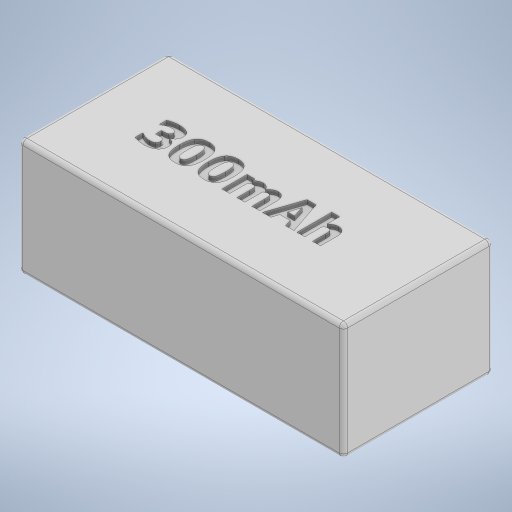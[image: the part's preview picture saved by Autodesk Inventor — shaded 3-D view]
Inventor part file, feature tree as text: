
AUTODESK INVENTOR PART (.ipt)
format: ipt  version: 2023.5 (Build 275446000, 446)  size: 368,640 bytes
history: native  units: mm
features: extrude x2, sketch x2, other x1, fillet x1
ambient origin geometry x8: Origin, YZ Plane, XZ Plane, XY Plane, X Axis, Y Axis, Z Axis, Center Point
bodies: Body1 (feature_tree)
feature tree (6):
  other  "Bryła1"
  extrude  "Wyciągnięcie proste1"  Depth=39.0mm
  extrude  "Wyciągnięcie proste2"  Depth=18.0mm
  fillet  "Zaokrąglenie1"  Radius=14.0mm
  sketch  "Szkic1"
  sketch  "Szkic2"
